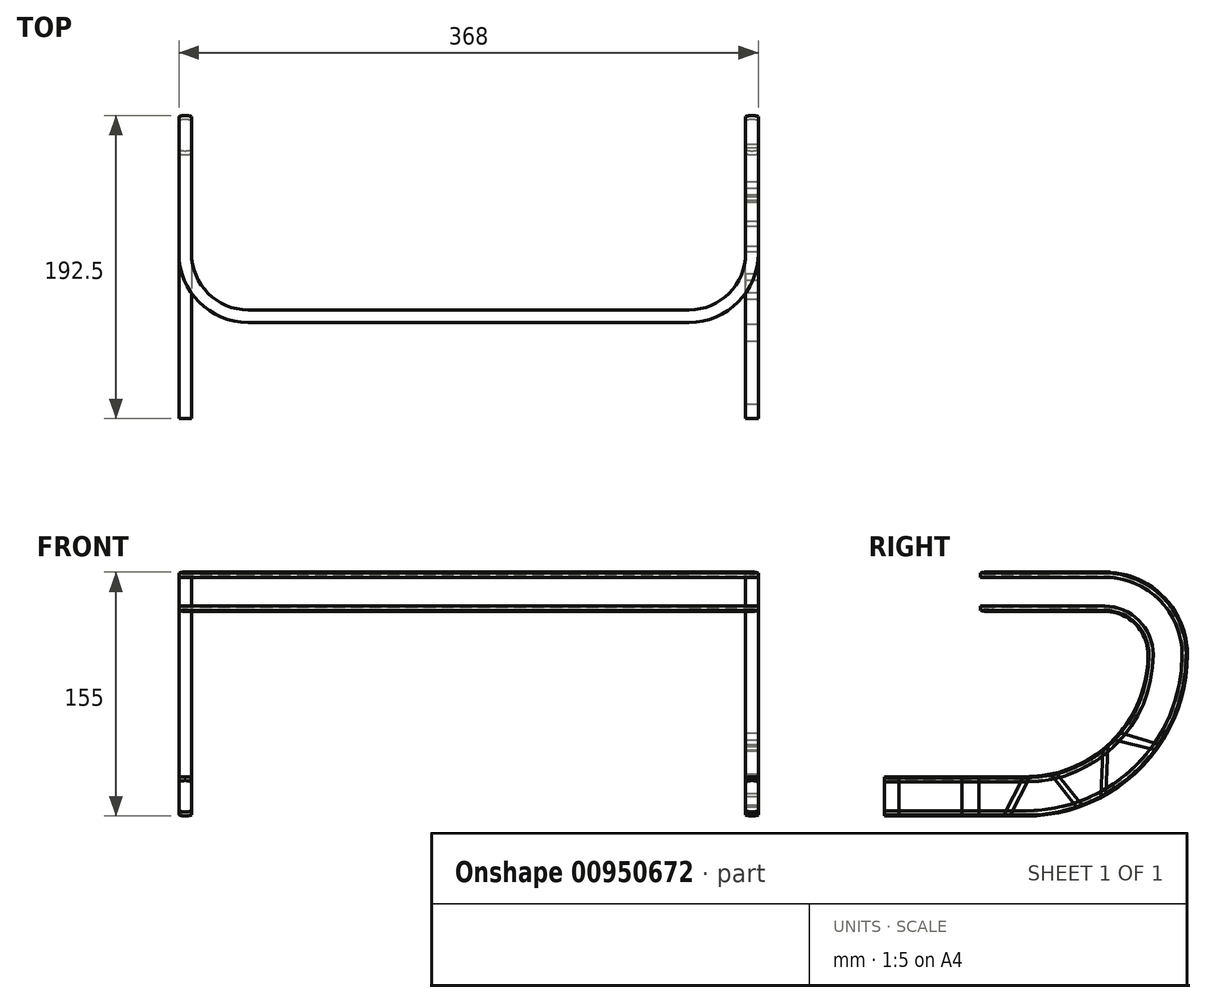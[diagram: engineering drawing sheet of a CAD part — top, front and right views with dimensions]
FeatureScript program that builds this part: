
annotation { "Feature Type Name" : "Feature", "Feature Type Description" : "" }
export const myFeature = defineFeature(function(context is Context, id is Id, definition is map)
    precondition{}
    {
        {
            var Q0;
            Q0=qCreatedBy(makeId("Top.planeOp"),FACE);
            var sketch = newSketch(context, id + "F0", { "sketchPlane" : qUnion([Q0])});
            skLineSegment(sketch, "E0", {"start": v(-140, 0) * mm, "end": v(140, 0) * mm});
            skArc(sketch, "E1", {"start": v(-180, 40) * mm, "mid": v(-168.28, 11.72) * mm, "end": v(-140, 0) * mm});
            skArc(sketch, "E2", {"start": v(140, 0) * mm, "mid": v(168.28, 11.72) * mm, "end": v(180, 40) * mm});
            skSolve(sketch);
        }
        {
            var Q0;
            Q0=qCreatedBy(makeId("Right.planeOp"),FACE);
            var Q1;
            Q1=sQuery(id+"F0.wireOp",VERTEX,"E2.end");
            cPlane(context, id + "F1", {"entities" : qUnion([Q0, Q1]), "cplaneType" : CPlaneType.PLANE_POINT, "offset" : 25 * mm, "width" : 150 * mm, "height" : 150 * mm});
        }
        {
            var Q0;
            Q0=qCreatedBy(id+"F1.planeOp",FACE);
            var sketch = newSketch(context, id + "F2", { "sketchPlane" : qUnion([Q0])});
            skPoint(sketch, "E3.0", {"position": v(40, 0) * mm});
            skLineSegment(sketch, "E4", {"start": v(40, 0) * mm, "end": v(75, 0) * mm});
            skArc(sketch, "E5", {"start": v(115, -40) * mm, "mid": v(103.28, -11.72) * mm, "end": v(75, 0) * mm});
            skArc(sketch, "E6", {"start": v(25, -130) * mm, "mid": v(88.64, -103.64) * mm, "end": v(115, -40) * mm});
            skLineSegment(sketch, "E7", {"start": v(25, -130) * mm, "end": v(-65, -130) * mm});
            skSolve(sketch);
        }
        {
            var Q0;
            Q0=sQuery(id+"F0.wireOp",VERTEX,"E1.start");
            var Q1;
            Q1=qCreatedBy(id+"F1.planeOp",FACE);
            cPlane(context, id + "F3", {"entities" : qUnion([Q0, Q1]), "cplaneType" : CPlaneType.PLANE_POINT, "offset" : 25 * mm, "width" : 150 * mm, "height" : 150 * mm});
        }
        {
            var Q0;
            Q0=qCreatedBy(id+"F3.planeOp",FACE);
            var sketch = newSketch(context, id + "F4", { "sketchPlane" : qUnion([Q0])});
            skLineSegment(sketch, "E8.0", {"start": v(40, 0) * mm, "end": v(75, 0) * mm});
            skArc(sketch, "E8.1", {"start": v(115, -40) * mm, "mid": v(103.28, -11.72) * mm, "end": v(75, 0) * mm});
            skArc(sketch, "E8.2", {"start": v(25, -130) * mm, "mid": v(88.64, -103.64) * mm, "end": v(115, -40) * mm});
            skLineSegment(sketch, "E8.3", {"start": v(25, -130) * mm, "end": v(-65, -130) * mm});
            skSolve(sketch);
        }
        {
            var Q0;
            Q0=qCreatedBy(makeId("Front.planeOp"),FACE);
            var Q1;
            Q1=sQuery(id+"F2.wireOp",VERTEX,"E7.end");
            cPlane(context, id + "F5", {"entities" : qUnion([Q0, Q1]), "cplaneType" : CPlaneType.PLANE_POINT, "offset" : 25 * mm, "width" : 150 * mm, "height" : 150 * mm});
        }
        {
            var Q0;
            Q0=qCreatedBy(id+"F5.planeOp",FACE);
            var sketch = newSketch(context, id + "F6", { "sketchPlane" : qUnion([Q0])});
            skPoint(sketch, "E9.0", {"position": v(180, -130) * mm});
            skArc(sketch, "E10", {"start": v(175.5, -141.66) * mm, "mid": v(175.75, -141.75) * mm, "end": v(176, -141.84) * mm, "construction": true});
            skArc(sketch, "E11", {"start": v(176, -139.17) * mm, "mid": v(180, -140) * mm, "end": v(184, -139.17) * mm, "construction": true});
            skArc(sketch, "E12.trimOffspring", {"start": v(184.5, -118.34) * mm, "mid": v(184.25, -118.25) * mm, "end": v(184, -118.16) * mm, "construction": true});
            skArc(sketch, "E13.trimOffspring", {"start": v(184, -120.83) * mm, "mid": v(180, -120) * mm, "end": v(176, -120.83) * mm, "construction": true});
            skArc(sketch, "E14.trimOffspring", {"start": v(176, -118.16) * mm, "mid": v(175.75, -118.25) * mm, "end": v(175.5, -118.34) * mm, "construction": true});
            skArc(sketch, "E15.trimOffspring", {"start": v(184, -141.84) * mm, "mid": v(184.25, -141.75) * mm, "end": v(184.5, -141.66) * mm, "construction": true});
            skArc(sketch, "E16", {"start": v(175.5, -116.26) * mm, "mid": v(165.54, -130) * mm, "end": v(175.5, -143.74) * mm});
            skArc(sketch, "E17.trimOffspring", {"start": v(184.5, -143.74) * mm, "mid": v(194.46, -130) * mm, "end": v(184.5, -116.26) * mm});
            skLineSegment(sketch, "E18", {"start": v(175.5, -116.26) * mm, "end": v(175.5, -118.34) * mm, "construction": true});
            skLineSegment(sketch, "E19", {"start": v(176, -118.16) * mm, "end": v(176, -120.83) * mm, "construction": true});
            skLineSegment(sketch, "E20", {"start": v(184.5, -116.26) * mm, "end": v(184.5, -118.34) * mm, "construction": true});
            skLineSegment(sketch, "E21", {"start": v(184, -118.16) * mm, "end": v(184, -120.83) * mm, "construction": true});
            skLineSegment(sketch, "E22", {"start": v(176, -141.84) * mm, "end": v(176, -139.17) * mm, "construction": true});
            skLineSegment(sketch, "E23", {"start": v(184, -141.84) * mm, "end": v(184, -139.17) * mm, "construction": true});
            skLineSegment(sketch, "E24", {"start": v(184.5, -143.74) * mm, "end": v(184.5, -141.66) * mm, "construction": true});
            skLineSegment(sketch, "E25", {"start": v(175.5, -116.26) * mm, "end": v(175.5, -118.34) * mm});
            skLineSegment(sketch, "E26", {"start": v(176, -118.16) * mm, "end": v(176, -120.83) * mm});
            skLineSegment(sketch, "E27", {"start": v(184.5, -116.26) * mm, "end": v(184.5, -118.34) * mm});
            skLineSegment(sketch, "E28", {"start": v(184.5, -118.34) * mm, "end": v(184, -118.16) * mm});
            skLineSegment(sketch, "E29", {"start": v(184, -118.16) * mm, "end": v(184, -120.83) * mm});
            skLineSegment(sketch, "E30", {"start": v(175.5, -143.74) * mm, "end": v(175.5, -141.66) * mm});
            skLineSegment(sketch, "E31", {"start": v(175.5, -141.66) * mm, "end": v(176, -141.84) * mm});
            skLineSegment(sketch, "E32", {"start": v(176, -141.84) * mm, "end": v(176, -139.17) * mm});
            skLineSegment(sketch, "E33", {"start": v(184, -139.17) * mm, "end": v(184, -141.84) * mm});
            skLineSegment(sketch, "E34", {"start": v(184, -141.84) * mm, "end": v(184.5, -141.66) * mm});
            skLineSegment(sketch, "E35", {"start": v(184.5, -141.66) * mm, "end": v(184.5, -143.74) * mm});
            skArc(sketch, "E36", {"start": v(176, -139.17) * mm, "mid": v(180, -140) * mm, "end": v(184, -139.17) * mm});
            skArc(sketch, "E37.trimOffspring", {"start": v(184, -120.83) * mm, "mid": v(180, -120) * mm, "end": v(176, -120.83) * mm});
            skCircle(sketch, "E38", {"center": v(180, -130) * mm, "radius": 12.5 * mm});
            skCircle(sketch, "E39", {"center": v(180, -130) * mm, "radius": 10 * mm});
            skLineSegment(sketch, "E40", {"start": v(176, -120.83) * mm, "end": v(176, -139.17) * mm});
            skLineSegment(sketch, "E41", {"start": v(184, -120.83) * mm, "end": v(184, -139.17) * mm});
            skLineSegment(sketch, "E42", {"start": v(175.5, -116.26) * mm, "end": v(175.5, -143.74) * mm});
            skLineSegment(sketch, "E43", {"start": v(184.5, -116.26) * mm, "end": v(184.5, -143.74) * mm});
            skCircle(sketch, "E44", {"center": v(180, -130) * mm, "radius": 14.46 * mm});
            skSolve(sketch);
        }
        {
            var Q0;
            {var subQ0=sQuery(id+"F6.wireOp",EDGE,"E17.trimOffspring");Q0=makeQuery(id+"F6.imprint","IMPRINT",FACE,{"disambiguationData":[TD([[makeQuery(id+"F6.imprint","IMPRINT",EDGE,{"derivedFrom":subQ0}),1.0]])]});}
            var Q1;
            {var subQ0=sQuery(id+"F6.wireOp",EDGE,"E16");Q1=makeQuery(id+"F6.imprint","IMPRINT",FACE,{"disambiguationData":[TD([[makeQuery(id+"F6.imprint","IMPRINT",EDGE,{"derivedFrom":subQ0}),1.0]])]});}
            var Q2;
            {var subQ0=sQuery(id+"F6.wireOp",EDGE,"E26");Q2=makeQuery(id+"F6.imprint","IMPRINT",FACE,{"disambiguationData":[TD([[makeQuery(id+"F6.imprint","IMPRINT",EDGE,{"derivedFrom":subQ0}),1.0]])]});}
            var Q3;
            {var subQ0=sQuery(id+"F6.wireOp",EDGE,"E32");Q3=makeQuery(id+"F6.imprint","IMPRINT",FACE,{"disambiguationData":[TD([[makeQuery(id+"F6.imprint","IMPRINT",EDGE,{"derivedFrom":subQ0}),-1.0]])]});}
            var Q4;
            Q4=sQuery(id+"F2.wireOp",EDGE,"E7");
            var Q5;
            Q5=sQuery(id+"F2.wireOp",EDGE,"E6");
            var Q6;
            Q6=qConstructionFilter(qBodyType(qCreatedBy(id+"F0",EDGE),BodyType.WIRE),ConstructionObject.NO);
            var Q7;
            Q7=sQuery(id+"F2.wireOp",EDGE,"E5");
            var Q8;
            Q8=sQuery(id+"F2.wireOp",EDGE,"E4");
            var Q9;
            Q9=sQuery(id+"F4.wireOp",EDGE,"E8.0");
            var Q10;
            Q10=sQuery(id+"F4.wireOp",EDGE,"E8.1");
            var Q11;
            Q11=sQuery(id+"F4.wireOp",EDGE,"E8.2");
            var Q12;
            Q12=sQuery(id+"F4.wireOp",EDGE,"E8.3");
            sweep(context, id + "F7", {"profiles" : qUnion([Q0, Q1, Q2, Q3]), "path" : qUnion([Q4, Q5, Q6, Q7, Q8, Q9, Q10, Q11, Q12])});
        }
        {
            var Q0;
            Q0=makeQuery(id+"F7.opSweep","SWEPT_FACE",FACE,{"disambiguationData":[OSD([sQuery(id+"F2.wireOp",EDGE,"E7"),sQuery(id+"F6.wireOp",EDGE,"E33")])]});
            cPlane(context, id + "F8", {"entities" : qUnion([Q0]), "cplaneType" : CPlaneType.OFFSET, "offset" : 0 * mm, "width" : 150 * mm, "height" : 150 * mm});
        }
        {
            var Q0;
            Q0=qCreatedBy(id+"F8.planeOp",FACE);
            var sketch = newSketch(context, id + "F9", { "sketchPlane" : qUnion([Q0])});
            skPoint(sketch, "E45.0", {"position": v(-65, -118.16) * mm});
            skPoint(sketch, "E45.1", {"position": v(-65, -141.84) * mm});
            skLineSegment(sketch, "E46.bottom", {"start": v(-65, -118.16) * mm, "end": v(-55.68, -118.16) * mm});
            skLineSegment(sketch, "E46.top", {"start": v(-65, -141.84) * mm, "end": v(-55.68, -141.84) * mm});
            skLineSegment(sketch, "E46.left", {"start": v(-65, -118.16) * mm, "end": v(-65, -141.84) * mm});
            skLineSegment(sketch, "E46.right", {"start": v(-55.68, -118.16) * mm, "end": v(-55.68, -141.84) * mm});
            skLineSegment(sketch, "E47.bottom", {"start": v(-15.8, -118.16) * mm, "end": v(-4.9, -118.16) * mm});
            skLineSegment(sketch, "E47.top", {"start": v(-15.8, -141.84) * mm, "end": v(-4.9, -141.84) * mm});
            skLineSegment(sketch, "E47.left", {"start": v(-15.8, -118.16) * mm, "end": v(-15.8, -141.84) * mm});
            skLineSegment(sketch, "E47.right", {"start": v(-4.9, -118.16) * mm, "end": v(-4.9, -141.84) * mm});
            skLineSegment(sketch, "E48.0", {"start": v(-65, -118.16) * mm, "end": v(25, -118.16) * mm});
            skArc(sketch, "E48.1", {"start": v(25, -118.16) * mm, "mid": v(80.27, -95.27) * mm, "end": v(103.16, -40) * mm});
            skArc(sketch, "E48.2", {"start": v(103.16, -40) * mm, "mid": v(94.91, -20.09) * mm, "end": v(75, -11.84) * mm});
            skLineSegment(sketch, "E48.3", {"start": v(75, -11.84) * mm, "end": v(40, -11.84) * mm});
            skLineSegment(sketch, "E48.4", {"start": v(40, -11.84) * mm, "end": v(-4, -11.84) * mm});
            skLineSegment(sketch, "E48.5", {"start": v(40, 11.84) * mm, "end": v(-4, 11.84) * mm});
            skLineSegment(sketch, "E48.6", {"start": v(75, 11.84) * mm, "end": v(40, 11.84) * mm});
            skArc(sketch, "E48.7", {"start": v(126.84, -40) * mm, "mid": v(111.66, -3.34) * mm, "end": v(75, 11.84) * mm});
            skArc(sketch, "E48.8", {"start": v(25, -141.84) * mm, "mid": v(97.01, -112.01) * mm, "end": v(126.84, -40) * mm});
            skLineSegment(sketch, "E48.9", {"start": v(-65, -141.84) * mm, "end": v(25, -141.84) * mm});
            skLineSegment(sketch, "E49", {"start": v(10.92, -141.84) * mm, "end": v(22.93, -118.16) * mm});
            skLineSegment(sketch, "E50", {"start": v(22.93, -118.16) * mm, "end": v(27.1, -118.13) * mm});
            skLineSegment(sketch, "E51", {"start": v(27.1, -118.13) * mm, "end": v(15.07, -141.84) * mm});
            skLineSegment(sketch, "E52", {"start": v(41.05, -116.5) * mm, "end": v(57.17, -136.63) * mm});
            skLineSegment(sketch, "E53", {"start": v(57.17, -136.63) * mm, "end": v(60.51, -135.45) * mm});
            skLineSegment(sketch, "E54", {"start": v(60.51, -135.45) * mm, "end": v(44.66, -115.65) * mm});
            skLineSegment(sketch, "E55", {"start": v(72.6, -130.04) * mm, "end": v(73.89, -100.98) * mm});
            skLineSegment(sketch, "E56", {"start": v(73.89, -100.98) * mm, "end": v(77.2, -98.16) * mm});
            skLineSegment(sketch, "E57", {"start": v(77.2, -98.16) * mm, "end": v(75.87, -128.23) * mm});
            skLineSegment(sketch, "E58", {"start": v(81.27, -94.24) * mm, "end": v(107.04, -100.34) * mm});
            skLineSegment(sketch, "E59", {"start": v(107.04, -100.34) * mm, "end": v(109.4, -96.98) * mm});
            skLineSegment(sketch, "E60", {"start": v(109.4, -96.98) * mm, "end": v(85.4, -89.6) * mm});
            skLineSegment(sketch, "E61", {"start": v(85.4, -89.6) * mm, "end": v(81.27, -94.24) * mm});
            skSolve(sketch);
        }
        {
            var Q0;
            Q0=makeQuery(id+"F9.imprint","IMPRINT",FACE,{"disambiguationData":[TD([[makeQuery(id+"F9.imprint","IMPRINT",EDGE,{"derivedFrom":sQuery(id+"F9.wireOp",EDGE,"E46.bottom")}),-1.0]])]});
            var Q1;
            Q1=makeQuery(id+"F9.imprint","IMPRINT",FACE,{"disambiguationData":[TD([[makeQuery(id+"F9.imprint","IMPRINT",EDGE,{"derivedFrom":sQuery(id+"F9.wireOp",EDGE,"E47.bottom")}),-1.0]])]});
            var Q2;
            {var subQ0=sQuery(id+"F9.wireOp",EDGE,"E49");Q2=makeQuery(id+"F9.imprint","IMPRINT",FACE,{"disambiguationData":[TD([[makeQuery(id+"F9.imprint","IMPRINT",EDGE,{"derivedFrom":subQ0}),-1.0]])]});}
            var Q3;
            {var subQ0=sQuery(id+"F9.wireOp",EDGE,"E52");Q3=makeQuery(id+"F9.imprint","IMPRINT",FACE,{"disambiguationData":[TD([[makeQuery(id+"F9.imprint","IMPRINT",EDGE,{"derivedFrom":subQ0}),1.0]])]});}
            var Q4;
            {var subQ1=sQuery(id+"F9.wireOp",EDGE,"E55");Q4=makeQuery(id+"F9.imprint","IMPRINT",FACE,{"disambiguationData":[TD([[makeQuery(id+"F9.imprint","IMPRINT",EDGE,{"derivedFrom":subQ1}),-1.0]])]});}
            var Q5;
            {var subQ1=sQuery(id+"F9.wireOp",EDGE,"E58");Q5=makeQuery(id+"F9.imprint","IMPRINT",FACE,{"disambiguationData":[TD([[makeQuery(id+"F9.imprint","IMPRINT",EDGE,{"derivedFrom":subQ1}),1.0]])]});}
            var Q6;
            Q6=makeQuery(id+"F7.opSweep","SWEPT_FACE",FACE,{"disambiguationData":[OSD([sQuery(id+"F2.wireOp",EDGE,"E7"),sQuery(id+"F6.wireOp",EDGE,"E26")])]});
            extrude(context, id + "F10", {"entities" : qUnion([Q0, Q1, Q2, Q3, Q4, Q5]), "endBound" : BoundingType.UP_TO_SURFACE, "oppositeDirection" : true, "depth" : 25 * mm, "endBoundEntityFace" : qUnion([Q6]), "offsetDistance" : 25 * mm});
        }
    });
